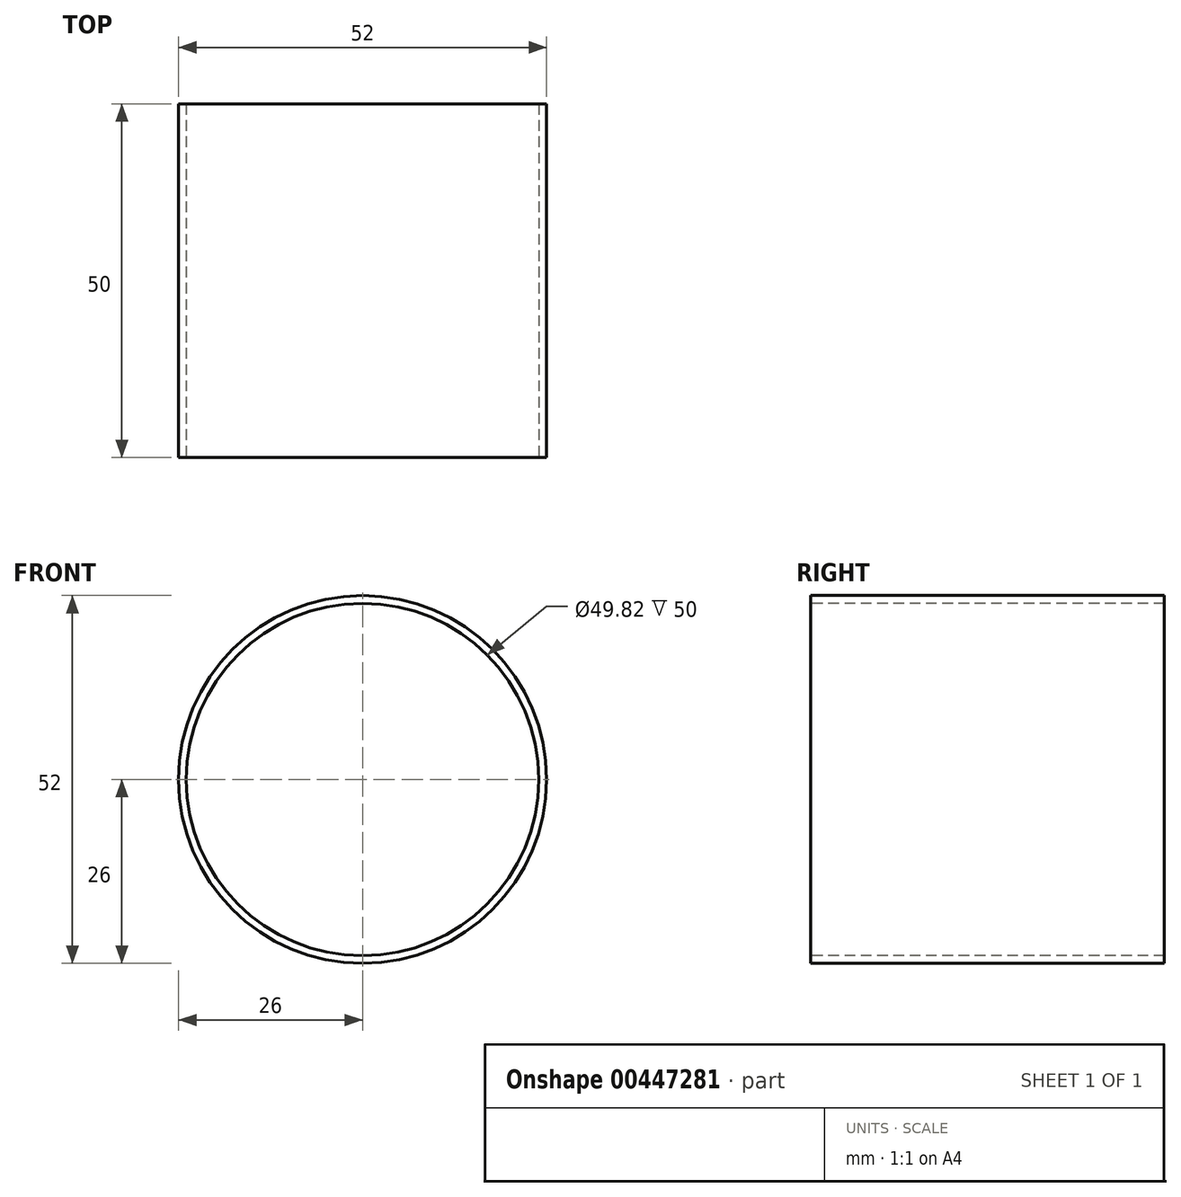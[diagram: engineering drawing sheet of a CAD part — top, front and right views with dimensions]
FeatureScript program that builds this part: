
annotation { "Feature Type Name" : "Feature", "Feature Type Description" : "" }
export const myFeature = defineFeature(function(context is Context, id is Id, definition is map)
    precondition{}
    {
        {
            var Q0;
            Q0=qCreatedBy(makeId("Front.planeOp"),FACE);
            var sketch = newSketch(context, id + "F0", { "sketchPlane" : qUnion([Q0])});
            skCircle(sketch, "E0", {"center": v(0, 0) * mm, "radius": 26 * mm});
            skSolve(sketch);
        }
        {
            var Q0;
            Q0=makeQuery(id+"F0.imprint","IMPRINT",FACE,{"disambiguationData":[TD([[makeQuery(id+"F0.imprint","IMPRINT",EDGE,{"derivedFrom":sQuery(id+"F0.wireOp",EDGE,"E0")}),1.0]])]});
            extrude(context, id + "F1", {"entities" : qUnion([Q0]), "depth" : 50 * mm});
        }
        {
            var Q0;
            Q0=makeQuery(id+"F1.opExtrude","CAP_FACE",FACE,{"disambiguationData":[OSD([sQuery(id+"F0.wireOp",EDGE,"E0")])],"isStart":false});
            var sketch = newSketch(context, id + "F2", { "sketchPlane" : qUnion([Q0])});
            skCircle(sketch, "E1", {"center": v(0, 0) * mm, "radius": 24.9 * mm});
            skSolve(sketch);
        }
        {
            var Q0;
            Q0=makeQuery(id+"F2.imprint","IMPRINT",FACE,{"disambiguationData":[TD([[makeQuery(id+"F2.imprint","IMPRINT",EDGE,{"derivedFrom":sQuery(id+"F2.wireOp",EDGE,"E1")}),1.0]])]});
            var Q1;
            Q1=sQuery(id+"F2.wireOp",EDGE,"E1");
            extrude(context, id + "F3", {"entities" : qUnion([Q0]), "operationType" : NewBodyOperationType.REMOVE, "surfaceEntities" : qUnion([Q1]), "endBound" : BoundingType.THROUGH_ALL, "oppositeDirection" : true, "depth" : 50 * mm});
        }
    });
